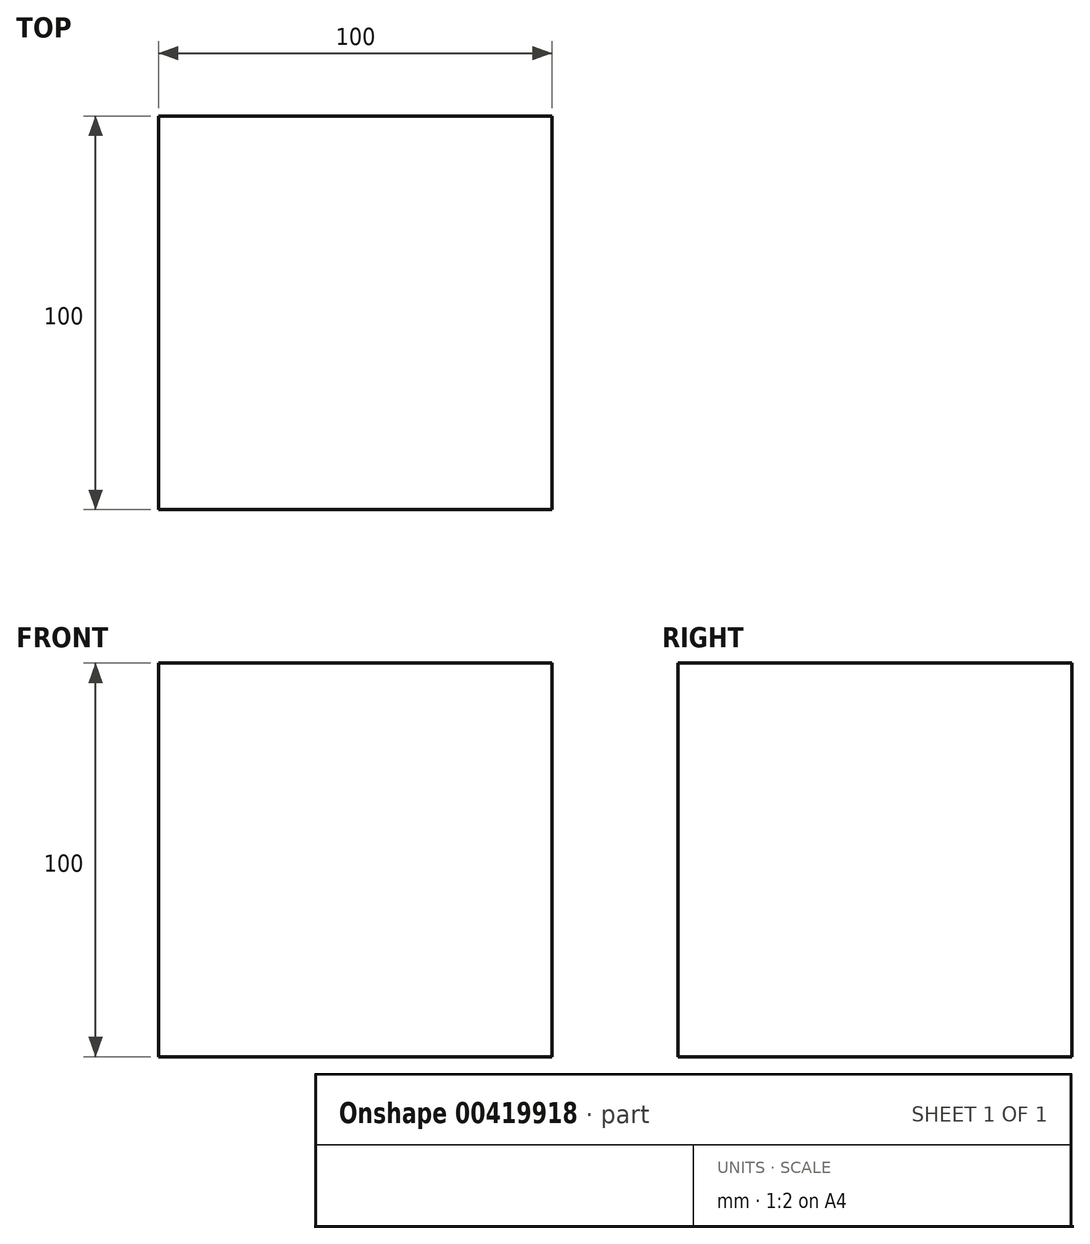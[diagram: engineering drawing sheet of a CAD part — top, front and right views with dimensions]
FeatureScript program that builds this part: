
annotation { "Feature Type Name" : "Feature", "Feature Type Description" : "" }
export const myFeature = defineFeature(function(context is Context, id is Id, definition is map)
    precondition{}
    {
        {
            var Q0;
            Q0=qCreatedBy(makeId("Top.planeOp"),FACE);
            var sketch = newSketch(context, id + "F0", { "sketchPlane" : qUnion([Q0])});
            skLineSegment(sketch, "E0.bottom", {"start": v(0, 0) * mm, "end": v(100, 0) * mm});
            skLineSegment(sketch, "E0.top", {"start": v(0, 100) * mm, "end": v(100, 100) * mm});
            skLineSegment(sketch, "E0.left", {"start": v(0, 0) * mm, "end": v(0, 100) * mm});
            skLineSegment(sketch, "E0.right", {"start": v(100, 0) * mm, "end": v(100, 100) * mm});
            skSolve(sketch);
        }
        {
            var Q0;
            Q0=qSketchRegion(id+"F0",true);
            extrude(context, id + "F1", {"entities" : qUnion([Q0]), "depth" : 100 * mm, "offsetDistance" : 25 * mm});
        }
    });
